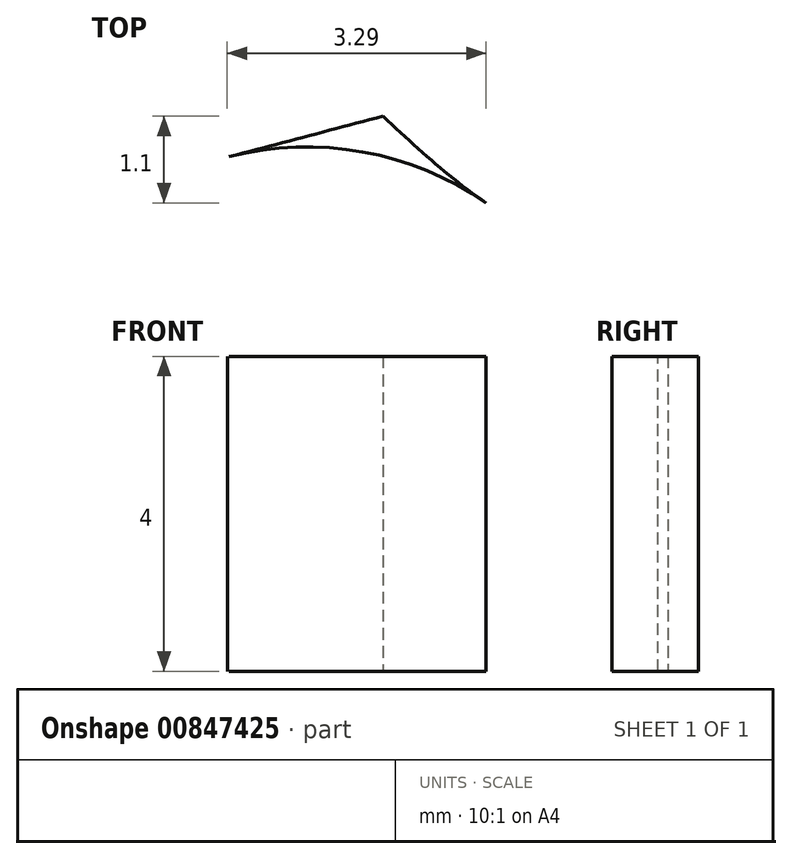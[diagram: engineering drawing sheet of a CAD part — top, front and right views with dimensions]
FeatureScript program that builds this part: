
annotation { "Feature Type Name" : "Feature", "Feature Type Description" : "" }
export const myFeature = defineFeature(function(context is Context, id is Id, definition is map)
    precondition{}
    {
        {
            var Q0;
            Q0=qCreatedBy(makeId("Top.planeOp"),FACE);
            var sketch = newSketch(context, id + "F0", { "sketchPlane" : qUnion([Q0])});
            skFitSpline(sketch, "E0", {"points": [v(7, 6.02) * mm, v(0, 8.45) * mm], "startDerivative": vector(-12.57, 0) * mm, "endDerivative": vector(-4.52, 4.26) * mm});
            skLineSegment(sketch, "E1", {"start": v(7, 6.02) * mm, "end": v(33.18, 7.43) * mm});
            skLineSegment(sketch, "E2", {"start": v(40.84, 1.88) * mm, "end": v(35.32, 6.7) * mm});
            skPoint(sketch, "E3.visualSharp", {"position": v(34.4, 7.5) * mm});
            skArc(sketch, "E3.filletArc", {"start": v(35.32, 6.7) * mm, "mid": v(34.32, 7.28) * mm, "end": v(33.18, 7.43) * mm});
            skLineSegment(sketch, "E4", {"start": v(-28.5, 0) * mm, "end": v(-28.5, 7) * mm});
            skFitSpline(sketch, "E5", {"points": [v(0, 8.45) * mm, v(-18.8, 4.95) * mm, v(-28.5, 7) * mm], "startDerivative": vector(-35, -9.2) * mm, "endDerivative": vector(-21.25, 7.18) * mm});
            skArc(sketch, "E6.filletArc", {"start": v(1.31, 7.35) * mm, "mid": v(-0.27, 8) * mm, "end": v(-1.98, 7.93) * mm});
            skArc(sketch, "E7.MirrorCS", {"start": v(35.32, -6.7) * mm, "mid": v(34.32, -7.28) * mm, "end": v(33.18, -7.43) * mm});
            skArc(sketch, "E8.MirrorCS", {"start": v(1.31, -7.35) * mm, "mid": v(-0.27, -8) * mm, "end": v(-1.98, -7.93) * mm});
            skLineSegment(sketch, "E9.MirrorCS", {"start": v(7, -6.02) * mm, "end": v(33.18, -7.43) * mm});
            skLineSegment(sketch, "E10.MirrorCS", {"start": v(40.84, -1.88) * mm, "end": v(35.32, -6.7) * mm});
            skPoint(sketch, "E11.MirrorP", {"position": v(0, -8.45) * mm});
            skPoint(sketch, "E12.MirrorP", {"position": v(34.4, -7.5) * mm});
            skLineSegment(sketch, "E13.MirrorCS", {"start": v(-28.5, 0) * mm, "end": v(-28.5, -7) * mm});
            skFitSpline(sketch, "E14.MirrorCS", {"points": [v(7, -6.02) * mm, v(0, -8.45) * mm], "startDerivative": vector(-12.57, 0) * mm, "endDerivative": vector(-4.52, -4.26) * mm});
            skFitSpline(sketch, "E15.MirrorCS", {"points": [v(0, -8.45) * mm, v(-18.8, -4.95) * mm, v(-28.5, -7) * mm], "startDerivative": vector(-35, 9.2) * mm, "endDerivative": vector(-21.25, -7.18) * mm});
            skPoint(sketch, "E16.visualSharp", {"position": v(43, 0) * mm});
            skArc(sketch, "E16.filletArc", {"start": v(40.84, -1.88) * mm, "mid": v(41.7, 0) * mm, "end": v(40.84, 1.88) * mm});
            skLineSegment(sketch, "E17", {"start": v(34.4, -7.5) * mm, "end": v(34.4, 7.5) * mm, "construction": true});
            skLineSegment(sketch, "E18", {"start": v(43, 0) * mm, "end": v(28.57, 0) * mm, "construction": true});
            skSolve(sketch);
        }
        {
            var Q0;
            Q0=makeQuery(id+"F0.imprint","IMPRINT",FACE,{"disambiguationData":[TD([[makeQuery(id+"F0.imprint","IMPRINT",EDGE,{"derivedFrom":sQuery(id+"F0.wireOp",EDGE,"E0")}),1.0]])]});
            extrude(context, id + "F1", {"entities" : qUnion([Q0]), "depth" : 4 * mm, "offsetDistance" : 25 * mm});
        }
    });
